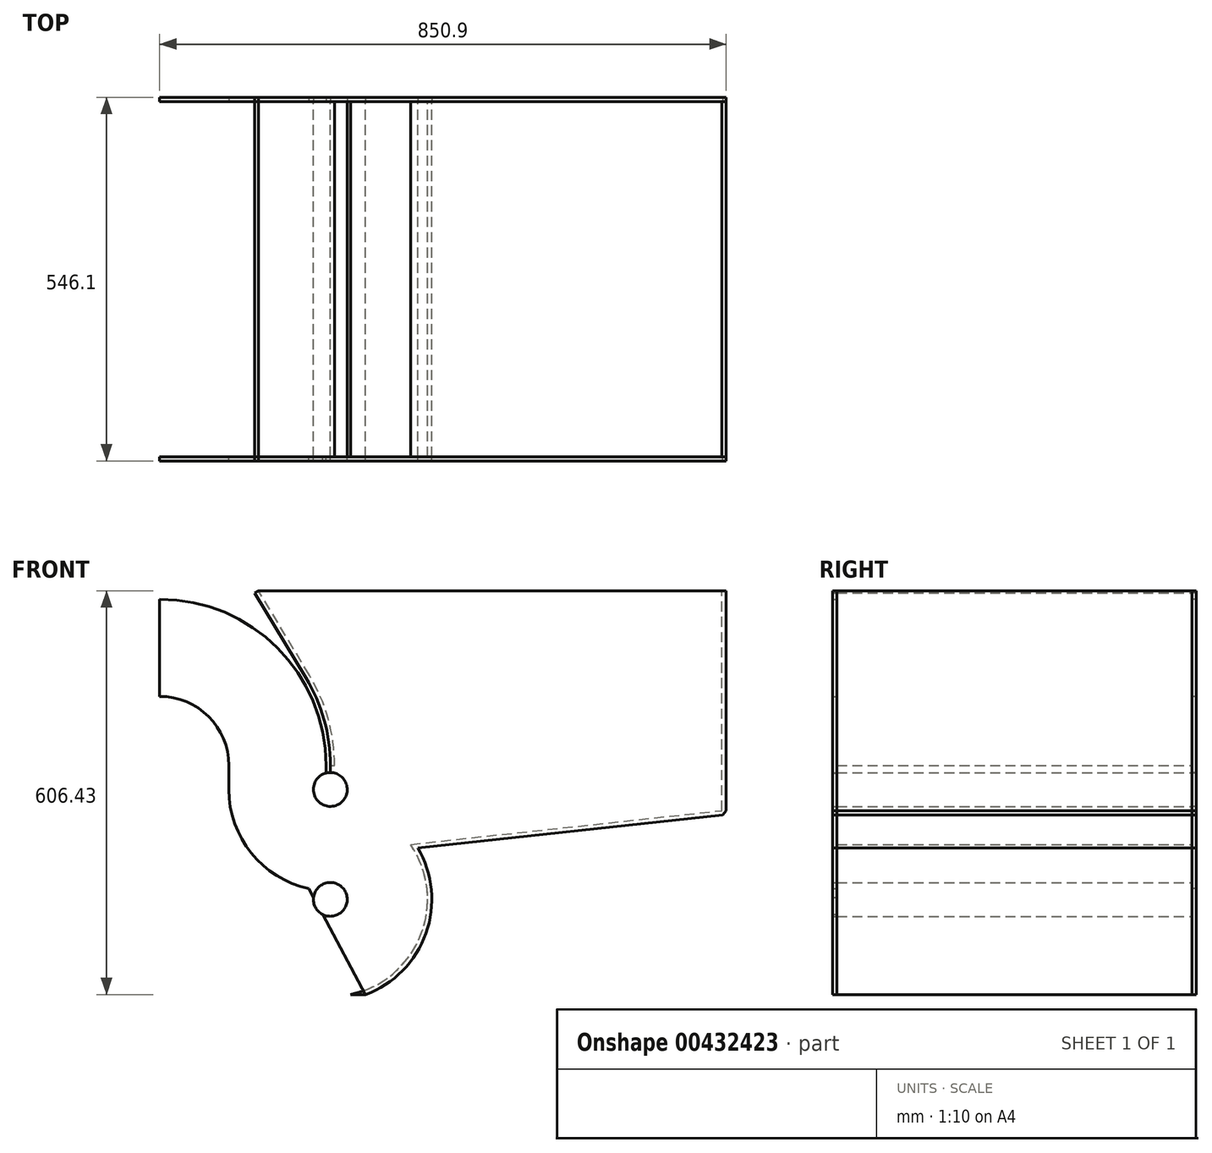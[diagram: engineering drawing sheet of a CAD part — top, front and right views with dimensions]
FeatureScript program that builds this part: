
annotation { "Feature Type Name" : "Feature", "Feature Type Description" : "" }
export const myFeature = defineFeature(function(context is Context, id is Id, definition is map)
    precondition{}
    {
        {
            var Q0;
            Q0=qCreatedBy(makeId("Front.planeOp"),FACE);
            var sketch = newSketch(context, id + "F0", { "sketchPlane" : qUnion([Q0])});
            skCircle(sketch, "E0", {"center": v(0, 146.05) * mm, "radius": 25.4 * mm});
            skArc(sketch, "E1", {"start": v(30.29, 3.18) * mm, "mid": v(135.6, 91.8) * mm, "end": v(120.48, 228.6) * mm});
            skCircle(sketch, "E2", {"center": v(0, 311.15) * mm, "radius": 25.4 * mm});
            skArc(sketch, "E3", {"start": v(-30.86, 168.4) * mm, "mid": v(-113.66, 219.43) * mm, "end": v(-146.05, 311.15) * mm});
            skLineSegment(sketch, "E4", {"start": v(-146.05, 311.15) * mm, "end": v(-146.05, 347.07) * mm});
            skLineSegment(sketch, "E5", {"start": v(-822.38, 0) * mm, "end": v(999.77, 0) * mm, "construction": true});
            skArc(sketch, "E6", {"start": v(-146.05, 347.07) * mm, "mid": v(-178.3, 424.94) * mm, "end": v(-256.18, 457.2) * mm});
            skArc(sketch, "E7", {"start": v(-256.18, 590.55) * mm, "mid": v(-84.01, 519.24) * mm, "end": v(-12.7, 347.07) * mm});
            skLineSegment(sketch, "E8.bottom", {"start": v(-338.73, 0) * mm, "end": v(677.27, 0) * mm, "construction": true});
            skLineSegment(sketch, "E8.top", {"start": v(-338.73, 609.6) * mm, "end": v(677.27, 609.6) * mm, "construction": true});
            skLineSegment(sketch, "E8.left", {"start": v(-338.73, 0) * mm, "end": v(-338.73, 609.6) * mm, "construction": true});
            skLineSegment(sketch, "E8.right", {"start": v(677.27, 0) * mm, "end": v(677.27, 609.6) * mm, "construction": true});
            skLineSegment(sketch, "E9", {"start": v(120.48, 228.6) * mm, "end": v(588.37, 279.4) * mm});
            skLineSegment(sketch, "E10", {"start": v(588.37, 279.4) * mm, "end": v(588.37, 609.6) * mm});
            skArc(sketch, "E11", {"start": v(6.35, 347.07) * mm, "mid": v(-3.25, 417.4) * mm, "end": v(-31.34, 482.6) * mm});
            skLineSegment(sketch, "E12", {"start": v(-31.34, 482.6) * mm, "end": v(-107.9, 609.6) * mm});
            skLineSegment(sketch, "E13", {"start": v(-107.9, 609.6) * mm, "end": v(588.37, 609.6) * mm});
            skArc(sketch, "E14.0", {"start": v(53.03, 3.18) * mm, "mid": v(143.6, 95) * mm, "end": v(131.32, 223.39) * mm});
            skLineSegment(sketch, "E15.0", {"start": v(131.32, 223.39) * mm, "end": v(589.06, 273.09) * mm});
            skLineSegment(sketch, "E16.0", {"start": v(594.72, 279.4) * mm, "end": v(594.72, 609.6) * mm});
            skLineSegment(sketch, "E17.0", {"start": v(-36.78, 479.32) * mm, "end": v(-113.33, 606.32) * mm});
            skArc(sketch, "E18.0", {"start": v(0, 347.07) * mm, "mid": v(-9.37, 415.7) * mm, "end": v(-36.78, 479.32) * mm});
            skArc(sketch, "E19.0", {"start": v(-256.18, 596.9) * mm, "mid": v(-79.52, 523.73) * mm, "end": v(-6.35, 347.07) * mm});
            skArc(sketch, "E20.0", {"start": v(-152.4, 347.07) * mm, "mid": v(-182.8, 420.45) * mm, "end": v(-256.18, 450.85) * mm});
            skArc(sketch, "E21.0", {"start": v(-32.2, 162.2) * mm, "mid": v(-118.6, 215.45) * mm, "end": v(-152.4, 311.15) * mm});
            skLineSegment(sketch, "E22.0", {"start": v(-152.4, 311.15) * mm, "end": v(-152.4, 347.07) * mm});
            skLineSegment(sketch, "E23", {"start": v(30.29, 3.18) * mm, "end": v(53.03, 3.18) * mm});
            skLineSegment(sketch, "E24", {"start": v(-32.2, 162.2) * mm, "end": v(-30.86, 168.4) * mm});
            skLineSegment(sketch, "E25", {"start": v(-256.18, 450.85) * mm, "end": v(-256.18, 457.2) * mm});
            skLineSegment(sketch, "E26", {"start": v(-256.18, 596.9) * mm, "end": v(-256.18, 590.55) * mm});
            skLineSegment(sketch, "E27", {"start": v(-6.35, 347.07) * mm, "end": v(-12.7, 347.07) * mm});
            skLineSegment(sketch, "E28", {"start": v(0, 347.07) * mm, "end": v(6.35, 347.07) * mm});
            skLineSegment(sketch, "E29", {"start": v(-113.33, 606.32) * mm, "end": v(-107.9, 609.6) * mm});
            skLineSegment(sketch, "E30", {"start": v(589.06, 273.09) * mm, "end": v(594.72, 279.4) * mm});
            skLineSegment(sketch, "E31", {"start": v(594.72, 609.6) * mm, "end": v(588.37, 609.6) * mm});
            skSolve(sketch);
        }
        {
            var Q0;
            Q0=makeQuery(id+"F0.imprint","IMPRINT",FACE,{"disambiguationData":[TD([[makeQuery(id+"F0.imprint","IMPRINT",EDGE,{"derivedFrom":sQuery(id+"F0.wireOp",EDGE,"E0")}),1.0]])]});
            var Q1;
            Q1=makeQuery(id+"F0.imprint","IMPRINT",FACE,{"disambiguationData":[TD([[makeQuery(id+"F0.imprint","IMPRINT",EDGE,{"derivedFrom":sQuery(id+"F0.wireOp",EDGE,"E3")}),1.0]])]});
            var Q2;
            Q2=makeQuery(id+"F0.imprint","IMPRINT",FACE,{"disambiguationData":[TD([[makeQuery(id+"F0.imprint","IMPRINT",EDGE,{"derivedFrom":sQuery(id+"F0.wireOp",EDGE,"E2")}),1.0]])]});
            var Q3;
            Q3=makeQuery(id+"F0.imprint","IMPRINT",FACE,{"disambiguationData":[TD([[makeQuery(id+"F0.imprint","IMPRINT",EDGE,{"derivedFrom":sQuery(id+"F0.wireOp",EDGE,"E11")}),1.0]])]});
            var Q4;
            Q4=makeQuery(id+"F0.imprint","IMPRINT",FACE,{"disambiguationData":[TD([[makeQuery(id+"F0.imprint","IMPRINT",EDGE,{"derivedFrom":sQuery(id+"F0.wireOp",EDGE,"E1")}),-1.0]])]});
            var Q5;
            Q5=makeQuery(id+"F0.imprint","IMPRINT",FACE,{"disambiguationData":[TD([[makeQuery(id+"F0.imprint","IMPRINT",EDGE,{"derivedFrom":sQuery(id+"F0.wireOp",EDGE,"E7")}),1.0]])]});
            extrude(context, id + "F1", {"entities" : qUnion([Q0, Q1, Q2, Q3, Q4, Q5]), "depth" : 533.4 * mm});
        }
        {
            var Q0;
            Q0=qCreatedBy(makeId("Front.planeOp"),FACE);
            var sketch = newSketch(context, id + "F2", { "sketchPlane" : qUnion([Q0])});
            skLineSegment(sketch, "E32.0", {"start": v(-36.78, 479.32) * mm, "end": v(-113.33, 606.32) * mm});
            skLineSegment(sketch, "E33.0", {"start": v(-107.9, 609.6) * mm, "end": v(588.37, 609.6) * mm});
            skLineSegment(sketch, "E34.0", {"start": v(594.72, 279.4) * mm, "end": v(594.72, 609.6) * mm});
            skLineSegment(sketch, "E35.0", {"start": v(131.32, 223.39) * mm, "end": v(589.06, 273.09) * mm});
            skArc(sketch, "E36.0", {"start": v(53.03, 3.18) * mm, "mid": v(143.6, 95) * mm, "end": v(131.32, 223.39) * mm});
            skArc(sketch, "E37.0", {"start": v(0, 347.07) * mm, "mid": v(-9.37, 415.7) * mm, "end": v(-36.78, 479.32) * mm});
            skArc(sketch, "E38.0", {"start": v(-256.18, 596.9) * mm, "mid": v(-79.52, 523.73) * mm, "end": v(-6.35, 347.07) * mm});
            skArc(sketch, "E39.0", {"start": v(-152.4, 347.07) * mm, "mid": v(-182.8, 420.45) * mm, "end": v(-256.18, 450.85) * mm});
            skArc(sketch, "E40.0", {"start": v(-32.2, 162.2) * mm, "mid": v(-118.6, 215.45) * mm, "end": v(-152.4, 311.15) * mm});
            skLineSegment(sketch, "E41.0", {"start": v(-152.4, 311.15) * mm, "end": v(-152.4, 347.07) * mm});
            skLineSegment(sketch, "E42", {"start": v(-256.18, 596.9) * mm, "end": v(-256.18, 450.85) * mm});
            skLineSegment(sketch, "E43", {"start": v(-32.2, 162.2) * mm, "end": v(53.03, 3.17) * mm});
            skLineSegment(sketch, "E44", {"start": v(-113.33, 606.32) * mm, "end": v(-107.9, 609.6) * mm});
            skLineSegment(sketch, "E45", {"start": v(588.37, 609.6) * mm, "end": v(594.72, 609.6) * mm});
            skLineSegment(sketch, "E46", {"start": v(589.06, 273.09) * mm, "end": v(594.72, 279.4) * mm});
            skArc(sketch, "E47", {"start": v(-6.35, 335.74) * mm, "mid": v(3.2, 285.95) * mm, "end": v(0, 336.55) * mm});
            skLineSegment(sketch, "E48", {"start": v(-6.35, 347.07) * mm, "end": v(-6.35, 335.74) * mm});
            skLineSegment(sketch, "E49", {"start": v(0, 347.07) * mm, "end": v(0, 336.55) * mm});
            skSolve(sketch);
        }
        {
            var Q0;
            Q0=makeQuery(id+"F2.imprint","IMPRINT",FACE,{"disambiguationData":[TD([[makeQuery(id+"F2.imprint","IMPRINT",EDGE,{"derivedFrom":sQuery(id+"F2.wireOp",EDGE,"E32.0")}),-1.0]])]});
            extrude(context, id + "F3", {"entities" : qUnion([Q0]), "oppositeDirection" : true, "depth" : 6.35 * mm});
        }
        {
            var Q0;
            Q0=makeQuery(id+"F1.opExtrude","CAP_FACE",FACE,{"disambiguationData":[OSD([sQuery(id+"F0.wireOp",EDGE,"E0")])],"isStart":false});
            var sketch = newSketch(context, id + "F4", { "sketchPlane" : qUnion([Q0])});
            skArc(sketch, "E50.0.0", {"start": v(-152.4, 311.15) * mm, "mid": v(-118.6, 215.45) * mm, "end": v(-32.2, 162.2) * mm});
            skLineSegment(sketch, "E50.0.1", {"start": v(-32.2, 162.2) * mm, "end": v(53.03, 3.17) * mm});
            skArc(sketch, "E50.0.2", {"start": v(53.03, 3.18) * mm, "mid": v(143.6, 95) * mm, "end": v(131.32, 223.39) * mm});
            skLineSegment(sketch, "E50.0.3", {"start": v(131.32, 223.39) * mm, "end": v(589.06, 273.09) * mm});
            skLineSegment(sketch, "E50.0.4", {"start": v(589.06, 273.09) * mm, "end": v(594.72, 279.4) * mm});
            skLineSegment(sketch, "E50.0.5", {"start": v(594.72, 279.4) * mm, "end": v(594.72, 609.6) * mm});
            skLineSegment(sketch, "E50.0.6", {"start": v(594.72, 609.6) * mm, "end": v(-107.9, 609.6) * mm});
            skLineSegment(sketch, "E50.0.7", {"start": v(-107.9, 609.6) * mm, "end": v(-113.33, 606.32) * mm});
            skLineSegment(sketch, "E50.0.8", {"start": v(-113.33, 606.32) * mm, "end": v(-36.78, 479.32) * mm});
            skLineSegment(sketch, "E50.0.9", {"start": v(-36.78, 479.32) * mm, "end": v(-36.78, 479.32) * mm});
            skArc(sketch, "E50.0.11", {"start": v(-44.23, 479.32) * mm, "mid": v(-134.99, 565.54) * mm, "end": v(-256.18, 596.9) * mm});
            skLineSegment(sketch, "E50.0.12", {"start": v(-256.18, 596.9) * mm, "end": v(-256.18, 450.85) * mm});
            skArc(sketch, "E50.0.13", {"start": v(-256.18, 450.85) * mm, "mid": v(-182.8, 420.45) * mm, "end": v(-152.4, 347.07) * mm});
            skLineSegment(sketch, "E50.0.14", {"start": v(-152.4, 347.07) * mm, "end": v(-152.4, 311.15) * mm});
            skLineSegment(sketch, "E51.0", {"start": v(-6.35, 347.07) * mm, "end": v(-6.35, 335.74) * mm});
            skLineSegment(sketch, "E52.0", {"start": v(0, 347.07) * mm, "end": v(0, 336.55) * mm});
            skArc(sketch, "E53.0", {"start": v(-6.35, 335.74) * mm, "mid": v(3.2, 285.95) * mm, "end": v(0, 336.55) * mm});
            skArc(sketch, "E54.0", {"start": v(-256.18, 596.9) * mm, "mid": v(-79.52, 523.73) * mm, "end": v(-6.35, 347.07) * mm});
            skArc(sketch, "E55.0", {"start": v(0, 347.07) * mm, "mid": v(-9.37, 415.7) * mm, "end": v(-36.78, 479.32) * mm});
            skSolve(sketch);
        }
        {
            var Q0;
            {var subQ0=sQuery(id+"F4.wireOp",EDGE,"E50.0.0");Q0=makeQuery(id+"F4.imprint","IMPRINT",FACE,{"disambiguationData":[TD([[makeQuery(id+"F4.imprint","IMPRINT",EDGE,{"derivedFrom":subQ0}),1.0]])]});}
            extrude(context, id + "F5", {"entities" : qUnion([Q0]), "depth" : 6.35 * mm});
        }
    });
